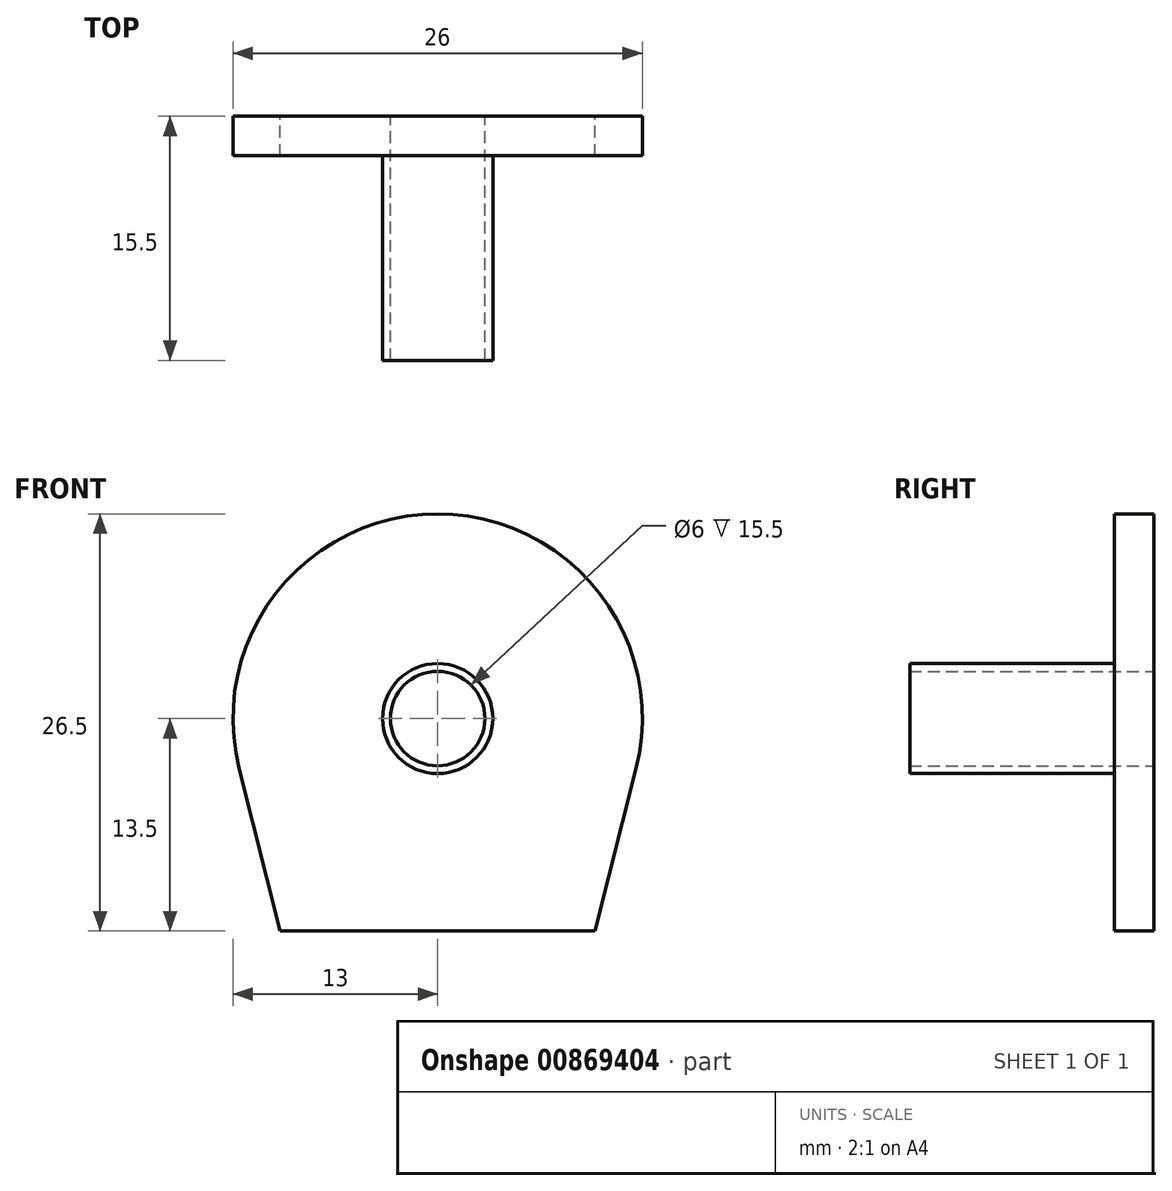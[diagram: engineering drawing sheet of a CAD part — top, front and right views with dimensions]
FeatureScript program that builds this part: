
annotation { "Feature Type Name" : "Feature", "Feature Type Description" : "" }
export const myFeature = defineFeature(function(context is Context, id is Id, definition is map)
    precondition{}
    {
        {
            var Q0;
            Q0=qCreatedBy(makeId("Front.planeOp"),FACE);
            var sketch = newSketch(context, id + "F0", { "sketchPlane" : qUnion([Q0])});
            skArc(sketch, "E0", {"start": v(12.6, -3.18) * mm, "mid": v(0, 13) * mm, "end": v(-12.6, -3.18) * mm});
            skCircle(sketch, "E1", {"center": v(0, 0) * mm, "radius": 3 * mm});
            skLineSegment(sketch, "E2", {"start": v(0, 0) * mm, "end": v(0, -13.5) * mm, "construction": true});
            skLineSegment(sketch, "E3", {"start": v(-10, -13.5) * mm, "end": v(10, -13.5) * mm});
            skLineSegment(sketch, "E4", {"start": v(10, -13.5) * mm, "end": v(12.6, -3.18) * mm});
            skLineSegment(sketch, "E5", {"start": v(-10, -13.5) * mm, "end": v(-12.6, -3.18) * mm});
            skSolve(sketch);
        }
        {
            var Q0;
            Q0=makeQuery(id+"F0.imprint","IMPRINT",FACE,{"disambiguationData":[TD([[makeQuery(id+"F0.imprint","IMPRINT",EDGE,{"derivedFrom":sQuery(id+"F0.wireOp",EDGE,"E0")}),1.0]])]});
            extrude(context, id + "F1", {"entities" : qUnion([Q0]), "depth" : 2.5 * mm, "offsetDistance" : 25 * mm});
        }
        {
            var Q0;
            Q0=makeQuery(id+"F1.opExtrude","CAP_FACE",FACE,{"disambiguationData":[OSD([sQuery(id+"F0.wireOp",EDGE,"E0"),sQuery(id+"F0.wireOp",EDGE,"E1"),sQuery(id+"F0.wireOp",EDGE,"E3"),sQuery(id+"F0.wireOp",EDGE,"E4"),sQuery(id+"F0.wireOp",EDGE,"E5")])],"isStart":false});
            var sketch = newSketch(context, id + "F2", { "sketchPlane" : qUnion([Q0])});
            skCircle(sketch, "E6", {"center": v(0, 0) * mm, "radius": 3.5 * mm});
            skCircle(sketch, "E7.0", {"center": v(0, 0) * mm, "radius": 3 * mm});
            skSolve(sketch);
        }
        {
            var Q0;
            Q0=makeQuery(id+"F2.imprint","IMPRINT",FACE,{"disambiguationData":[TD([[makeQuery(id+"F2.imprint","IMPRINT",EDGE,{"derivedFrom":sQuery(id+"F2.wireOp",EDGE,"E6")}),1.0]])]});
            extrude(context, id + "F3", {"entities" : qUnion([Q0]), "operationType" : NewBodyOperationType.ADD, "depth" : 13 * mm, "offsetDistance" : 25 * mm});
        }
    });
